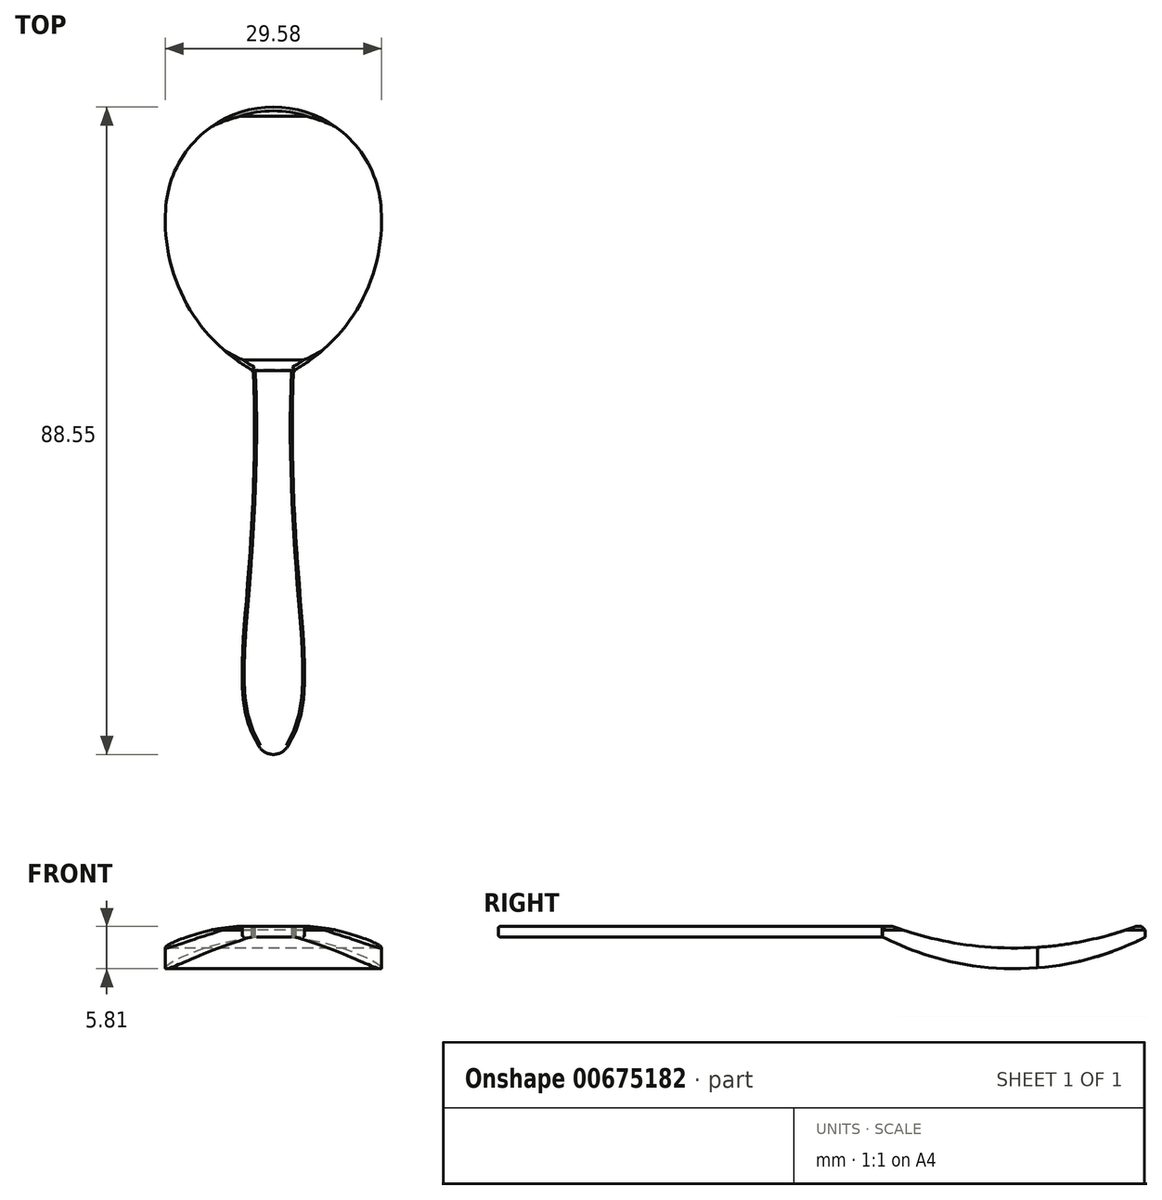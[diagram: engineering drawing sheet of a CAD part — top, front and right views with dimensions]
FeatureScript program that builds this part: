
annotation { "Feature Type Name" : "Feature", "Feature Type Description" : "" }
export const myFeature = defineFeature(function(context is Context, id is Id, definition is map)
    precondition{}
    {
        {
            var Q0;
            Q0=qCreatedBy(makeId("Top.planeOp"),FACE);
            var sketch = newSketch(context, id + "F0", { "sketchPlane" : qUnion([Q0])});
            skCircle(sketch, "E0", {"center": v(0, 49.26) * mm, "radius": 14.77 * mm});
            skLineSegment(sketch, "E1", {"start": v(0, 49.26) * mm, "end": v(-14.77, 49.26) * mm});
            skLineSegment(sketch, "E2", {"start": v(-14.77, 49.26) * mm, "end": v(14.77, 49.26) * mm});
            skLineSegment(sketch, "E3", {"start": v(0, 64.04) * mm, "end": v(0, 34.49) * mm});
            skArc(sketch, "E4", {"start": v(-14.77, 49.26) * mm, "mid": v(-10.97, 35.63) * mm, "end": v(0, 26.69) * mm});
            skArc(sketch, "E5.MirrorCS", {"start": v(14.77, 49.26) * mm, "mid": v(10.97, 35.63) * mm, "end": v(0, 26.69) * mm});
            skPoint(sketch, "E6", {"position": v(0, -35.85) * mm});
            skPoint(sketch, "E7", {"position": v(-2.96, 28.1) * mm});
            skPoint(sketch, "E8.MirrorP", {"position": v(2.96, 28.1) * mm});
            skFitSpline(sketch, "E9", {"points": [v(-2.96, 28.1) * mm, v(-2.96, 18.49) * mm, v(-3.4, 0) * mm, v(0, -35.85) * mm], "startDerivative": vector(-38.46, -46.78) * mm, "endDerivative": vector(35.21, -69.87) * mm});
            skFitSpline(sketch, "E10.MirrorCS", {"points": [v(2.96, 28.1) * mm, v(2.96, 18.49) * mm, v(3.4, 0) * mm, v(0, -35.85) * mm], "startDerivative": vector(38.46, -46.78) * mm, "endDerivative": vector(-35.21, -69.87) * mm});
            skLineSegment(sketch, "E11", {"start": v(0, 64.04) * mm, "end": v(0, -35.85) * mm});
            skLineSegment(sketch, "E12", {"start": v(2.96, 28.1) * mm, "end": v(34.32, 28.1) * mm});
            skLineSegment(sketch, "E13", {"start": v(34.32, 28.1) * mm, "end": v(-32.9, 28.1) * mm});
            skSolve(sketch);
        }
        {
            var Q0;
            Q0 = qSketchRegion(id + "F0", true);
            extrude(context, id + "F1", {"entities" : qUnion([Q0]), "depth" : 3.8 * mm, "offsetDistance" : 25.4 * mm, "hasSecondDirection" : true, "secondDirectionOppositeDirection" : true, "secondDirectionDepth" : 7.87 * mm});
        }
        {
            var Q0;
            Q0=qCreatedBy(makeId("Right.planeOp"),FACE);
            var sketch = newSketch(context, id + "F2", { "sketchPlane" : qUnion([Q0])});
            skLineSegment(sketch, "E14", {"start": v(64.2, 0) * mm, "end": v(64.2, 31.58) * mm});
            skLineSegment(sketch, "E15", {"start": v(28, 0) * mm, "end": v(28, 32.18) * mm});
            skLineSegment(sketch, "E16", {"start": v(64.2, 4.36) * mm, "end": v(28, 4.36) * mm});
            skArc(sketch, "E17", {"start": v(28, 4.36) * mm, "mid": v(46.1, 0.83) * mm, "end": v(64.2, 4.36) * mm});
            skLineSegment(sketch, "E18", {"start": v(64.2, 2.42) * mm, "end": v(28, 2.42) * mm});
            skArc(sketch, "E19", {"start": v(28, 2.42) * mm, "mid": v(46.1, -2) * mm, "end": v(64.2, 2.42) * mm});
            skSolve(sketch);
        }
        {
            var Q0;
            {var subQ0=sQuery(id+"F2.wireOp",EDGE,"E17");var subQ3=sQuery(id+"F2.wireOp",EDGE,"E18");var subQ5=makeQuery(id+"F2.imprint","INTERSECT",VERTEX,{"disambiguationData":[OD(1.0)],"derivedFrom":[subQ0,subQ3]});Q0=makeQuery(id+"F2.imprint","IMPRINT",FACE,{"disambiguationData":[TD([[makeQuery(id+"F2.imprint","IMPRINT",EDGE,{"disambiguationData":[TD([[subQ5,-1.0]])],"derivedFrom":subQ0}),-1.0]])]});}
            var Q1;
            {var subQ0=sQuery(id+"F2.wireOp",EDGE,"E17");var subQ3=sQuery(id+"F2.wireOp",EDGE,"E18");var subQ5=makeQuery(id+"F2.imprint","INTERSECT",VERTEX,{"disambiguationData":[OD(0.0)],"derivedFrom":[subQ0,subQ3]});Q1=makeQuery(id+"F2.imprint","IMPRINT",FACE,{"disambiguationData":[TD([[makeQuery(id+"F2.imprint","IMPRINT",EDGE,{"disambiguationData":[TD([[subQ5,1.0]])],"derivedFrom":subQ0}),-1.0]])]});}
            var Q2;
            {var subQ4=sQuery(id+"F2.wireOp",EDGE,"E19");Q2=makeQuery(id+"F2.imprint","IMPRINT",FACE,{"disambiguationData":[TD([[makeQuery(id+"F2.imprint","IMPRINT",EDGE,{"derivedFrom":subQ4}),1.0]])]});}
            extrude(context, id + "F3", {"entities" : qUnion([Q0, Q1, Q2]), "operationType" : NewBodyOperationType.INTERSECT, "endBound" : BoundingType.SYMMETRIC, "depth" : 37.08 * mm, "offsetDistance" : 25.4 * mm});
        }
        {
            var Q0;
            Q0=makeQuery(id+"F3.boolean.opBoolean","INTERSECT",EDGE,{"derivedFrom":[makeQuery(id+"F1.opExtrude","SWEPT_FACE",FACE,{"disambiguationData":[OSD([sQuery(id+"F0.wireOp",EDGE,"E4")])]}),makeQuery(id+"F3.boolean.toolComplement.opBoolean","COPY",FACE,{"derivedFrom":makeQuery(id+"F3.opExtrude","SWEPT_FACE",FACE,{"disambiguationData":[OSD([sQuery(id+"F2.wireOp",EDGE,"E17")])]})})]});
            var Q1;
            Q1=makeQuery(id+"F3.boolean.opBoolean","INTERSECT",EDGE,{"disambiguationData":[OD(0.0)],"derivedFrom":[makeQuery(id+"F1.opExtrude","SWEPT_FACE",FACE,{"disambiguationData":[OSD([sQuery(id+"F0.wireOp",EDGE,"E0")])]}),makeQuery(id+"F3.boolean.toolComplement.opBoolean","COPY",FACE,{"derivedFrom":makeQuery(id+"F3.opExtrude","SWEPT_FACE",FACE,{"disambiguationData":[OSD([sQuery(id+"F2.wireOp",EDGE,"E17")])]})})]});
            var Q2;
            Q2=makeQuery(id+"F3.boolean.opBoolean","INTERSECT",EDGE,{"derivedFrom":[makeQuery(id+"F1.opExtrude","SWEPT_FACE",FACE,{"disambiguationData":[OSD([sQuery(id+"F0.wireOp",EDGE,"E5.MirrorCS")])]}),makeQuery(id+"F3.boolean.toolComplement.opBoolean","COPY",FACE,{"derivedFrom":makeQuery(id+"F3.opExtrude","SWEPT_FACE",FACE,{"disambiguationData":[OSD([sQuery(id+"F2.wireOp",EDGE,"E17")])]})})]});
            var Q3;
            Q3=makeQuery(id+"F3.boolean.opBoolean","INTERSECT",EDGE,{"disambiguationData":[OD(1.0)],"derivedFrom":[makeQuery(id+"F1.opExtrude","SWEPT_FACE",FACE,{"disambiguationData":[OSD([sQuery(id+"F0.wireOp",EDGE,"E0")])]}),makeQuery(id+"F3.boolean.toolComplement.opBoolean","COPY",FACE,{"derivedFrom":makeQuery(id+"F3.opExtrude","SWEPT_FACE",FACE,{"disambiguationData":[OSD([sQuery(id+"F2.wireOp",EDGE,"E17")])]})})]});
            var Q4;
            Q4=makeQuery(id+"F1.opExtrude","CAP_EDGE",EDGE,{"disambiguationData":[OSD([sQuery(id+"F0.wireOp",EDGE,"E0")])],"isStart":false});
            var Q5;
            Q5=makeQuery(id+"F1.opExtrude","CAP_EDGE",EDGE,{"disambiguationData":[OSD([sQuery(id+"F0.wireOp",EDGE,"E5.MirrorCS")])],"isStart":false});
            var Q6;
            Q6=makeQuery(id+"F1.opExtrude","CAP_EDGE",EDGE,{"disambiguationData":[OSD([sQuery(id+"F0.wireOp",EDGE,"E4")])],"isStart":false});
            chamfer(context, id + "F4", {"entities" : qUnion([Q0, Q1, Q2, Q3, Q4, Q5, Q6]), "width" : 0.5 * mm, "tangentPropagation" : true});
        }
        {
            var Q0;
            Q0=qCreatedBy(makeId("Top.planeOp"),FACE);
            var sketch = newSketch(context, id + "F5", { "sketchPlane" : qUnion([Q0])});
            skLineSegment(sketch, "E20", {"start": v(0, 31.99) * mm, "end": v(0, -37.84) * mm});
            skFitSpline(sketch, "E21", {"points": [v(-2.74, 28.22) * mm, v(-2.57, 18.64) * mm, v(-3.43, 0) * mm, v(-3.94, -18.33) * mm, v(0, -26.61) * mm], "startDerivative": vector(1.6, -44.73) * mm, "endDerivative": vector(29.61, -48.52) * mm});
            skFitSpline(sketch, "E22.MirrorCS", {"points": [v(2.74, 28.22) * mm, v(2.57, 18.64) * mm, v(3.43, 0) * mm, v(3.94, -18.33) * mm, v(0, -26.61) * mm], "startDerivative": vector(-1.6, -44.73) * mm, "endDerivative": vector(-29.61, -48.52) * mm});
            skLineSegment(sketch, "E23", {"start": v(-2.74, 28.22) * mm, "end": v(2.74, 28.22) * mm});
            skArc(sketch, "E24", {"start": v(-2.03, -23.28) * mm, "mid": v(0, -24.5) * mm, "end": v(2.03, -23.28) * mm});
            skSolve(sketch);
        }
        {
            var Q0;
            {var subQ0=sQuery(id+"F5.wireOp",EDGE,"E23");var subQ1=sQuery(id+"F5.wireOp",EDGE,"E20");var subQ2=makeQuery(id+"F5.imprint","INTERSECT",VERTEX,{"derivedFrom":[subQ1,subQ0]});Q0=makeQuery(id+"F5.imprint","IMPRINT",FACE,{"disambiguationData":[TD([[makeQuery(id+"F5.imprint","IMPRINT",EDGE,{"disambiguationData":[TD([[subQ2,-1.0]])],"derivedFrom":subQ1}),-1.0]])]});}
            var Q1;
            {var subQ0=sQuery(id+"F5.wireOp",EDGE,"E23");var subQ1=sQuery(id+"F5.wireOp",EDGE,"E20");var subQ2=makeQuery(id+"F5.imprint","INTERSECT",VERTEX,{"derivedFrom":[subQ1,subQ0]});Q1=makeQuery(id+"F5.imprint","IMPRINT",FACE,{"disambiguationData":[TD([[makeQuery(id+"F5.imprint","IMPRINT",EDGE,{"disambiguationData":[TD([[subQ2,-1.0]])],"derivedFrom":subQ1}),1.0]])]});}
            extrude(context, id + "F6", {"entities" : qUnion([Q0, Q1]), "operationType" : NewBodyOperationType.ADD, "depth" : 3.78 * mm, "offsetDistance" : 25.4 * mm, "hasSecondDirection" : true, "secondDirectionOppositeDirection" : false, "secondDirectionDepth" : 2.36 * mm});
        }
        {
            var Q0;
            Q0=makeQuery(id+"F6.opExtrude","CAP_EDGE",EDGE,{"disambiguationData":[OSD([sQuery(id+"F5.wireOp",EDGE,"E21")])],"isStart":false});
            var Q1;
            Q1=makeQuery(id+"F6.opExtrude","CAP_EDGE",EDGE,{"disambiguationData":[OSD([sQuery(id+"F5.wireOp",EDGE,"E22.MirrorCS")])],"isStart":true});
            var Q2;
            Q2=makeQuery(id+"F6.opExtrude","CAP_EDGE",EDGE,{"disambiguationData":[OSD([sQuery(id+"F5.wireOp",EDGE,"E24")])],"isStart":false});
            var Q3;
            Q3=makeQuery(id+"F6.opExtrude","CAP_EDGE",EDGE,{"disambiguationData":[OSD([sQuery(id+"F5.wireOp",EDGE,"E21")])],"isStart":true});
            var Q4;
            Q4=makeQuery(id+"F6.opExtrude","CAP_EDGE",EDGE,{"disambiguationData":[OSD([sQuery(id+"F5.wireOp",EDGE,"E24")])],"isStart":true});
            fillet(context, id + "F7", {"entities" : qUnion([Q0, Q1, Q2, Q3, Q4]), "radius" : 0.25 * mm, "tangentPropagation" : true, "allowEdgeOverflow" : false});
        }
    });
